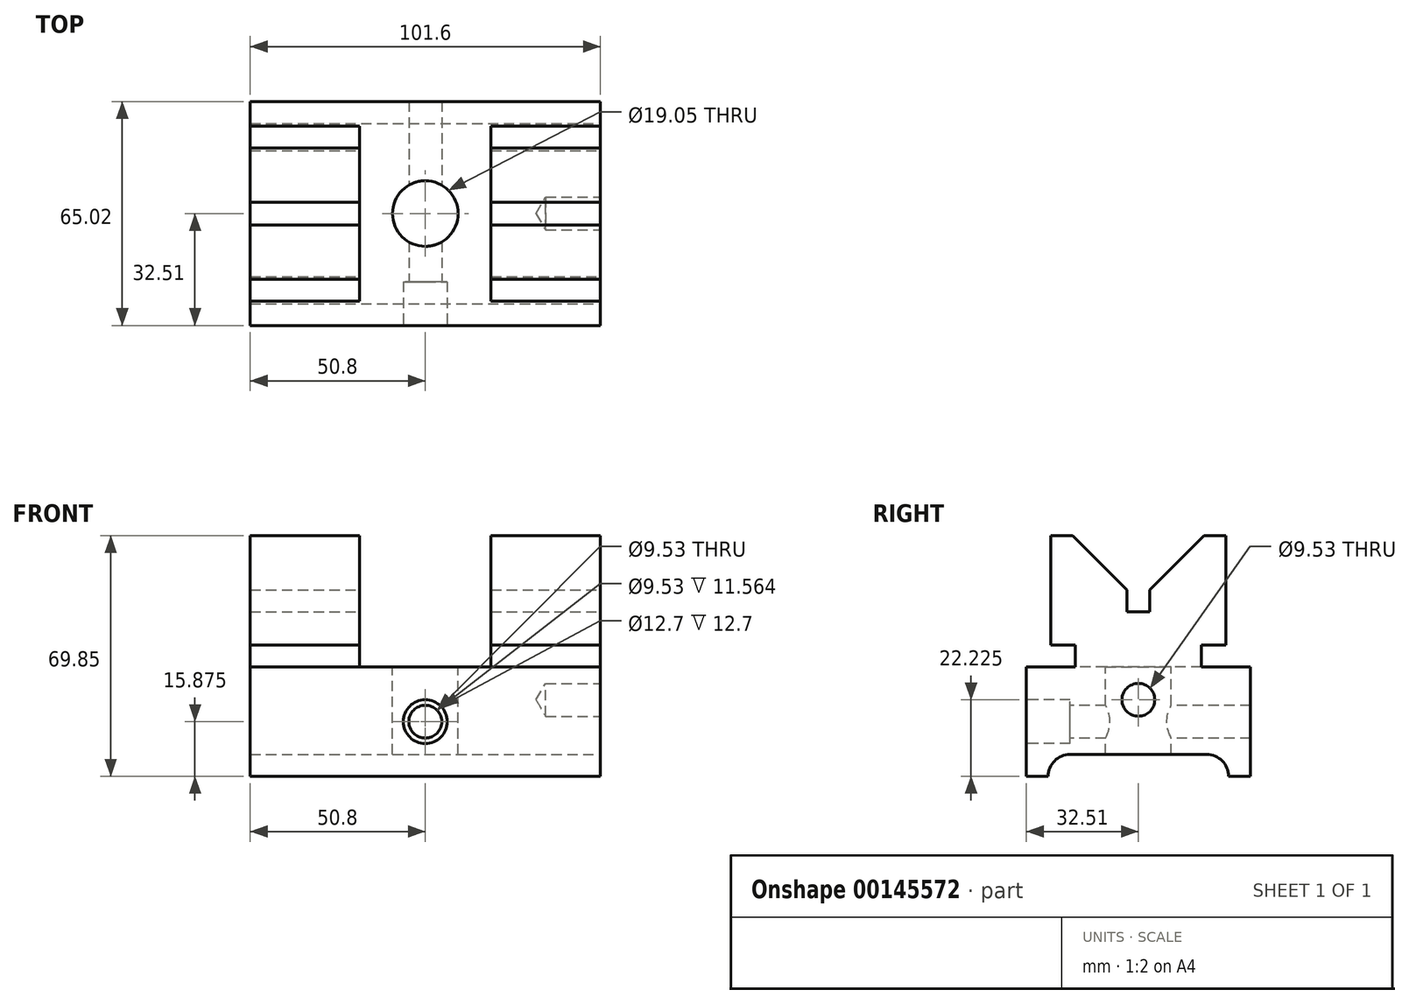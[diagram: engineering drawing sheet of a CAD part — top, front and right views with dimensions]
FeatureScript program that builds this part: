
annotation { "Feature Type Name" : "Feature", "Feature Type Description" : "" }
export const myFeature = defineFeature(function(context is Context, id is Id, definition is map)
    precondition{}
    {
        {
            var Q0;
            Q0=qCreatedBy(makeId("Right.planeOp"),FACE);
            var sketch = newSketch(context, id + "F0", { "sketchPlane" : qUnion([Q0])});
            skLineSegment(sketch, "E0", {"start": v(-32.51, 0) * mm, "end": v(-32.51, -31.75) * mm});
            skLineSegment(sketch, "E1", {"start": v(-32.51, -31.75) * mm, "end": v(-26.16, -31.75) * mm});
            skLineSegment(sketch, "E2", {"start": v(-26.16, -31.75) * mm, "end": v(-26.16, -31.75) * mm});
            skLineSegment(sketch, "E3", {"start": v(-19.81, -25.4) * mm, "end": v(19.81, -25.4) * mm});
            skLineSegment(sketch, "E4", {"start": v(26.16, -31.75) * mm, "end": v(26.16, -31.75) * mm});
            skLineSegment(sketch, "E5", {"start": v(26.16, -31.75) * mm, "end": v(32.51, -31.75) * mm});
            skLineSegment(sketch, "E6", {"start": v(32.51, -31.75) * mm, "end": v(32.51, 0) * mm});
            skLineSegment(sketch, "E7", {"start": v(32.51, 0) * mm, "end": v(18.29, 0) * mm});
            skLineSegment(sketch, "E8", {"start": v(18.29, 0) * mm, "end": v(18.29, 6.35) * mm});
            skLineSegment(sketch, "E9", {"start": v(-32.51, 0) * mm, "end": v(-18.29, 0) * mm});
            skLineSegment(sketch, "E10", {"start": v(-18.29, 0) * mm, "end": v(-18.29, 6.35) * mm});
            skPoint(sketch, "E11", {"position": v(0, -25.4) * mm});
            skLineSegment(sketch, "E12", {"start": v(18.29, 6.35) * mm, "end": v(25.4, 6.35) * mm});
            skLineSegment(sketch, "E13", {"start": v(25.4, 6.35) * mm, "end": v(25.4, 38.1) * mm});
            skLineSegment(sketch, "E14", {"start": v(25.4, 38.1) * mm, "end": v(19.05, 38.1) * mm});
            skLineSegment(sketch, "E15", {"start": v(19.05, 38.1) * mm, "end": v(3.3, 22.35) * mm});
            skLineSegment(sketch, "E16", {"start": v(3.3, 22.35) * mm, "end": v(3.3, 16) * mm});
            skLineSegment(sketch, "E17", {"start": v(3.3, 16) * mm, "end": v(-3.3, 16) * mm});
            skLineSegment(sketch, "E18", {"start": v(-3.3, 16) * mm, "end": v(-3.3, 22.35) * mm});
            skLineSegment(sketch, "E19", {"start": v(-3.3, 22.35) * mm, "end": v(-19.05, 38.1) * mm});
            skLineSegment(sketch, "E20", {"start": v(-19.05, 38.1) * mm, "end": v(-25.4, 38.1) * mm});
            skLineSegment(sketch, "E21", {"start": v(-25.4, 38.1) * mm, "end": v(-25.4, 6.35) * mm});
            skLineSegment(sketch, "E22", {"start": v(-25.4, 6.35) * mm, "end": v(-18.29, 6.35) * mm});
            skPoint(sketch, "E23", {"position": v(0, 16) * mm});
            skPoint(sketch, "E24.visualSharp", {"position": v(-26.16, -25.4) * mm});
            skArc(sketch, "E24.filletArc", {"start": v(-19.81, -25.4) * mm, "mid": v(-24.3, -27.26) * mm, "end": v(-26.16, -31.75) * mm});
            skPoint(sketch, "E25.visualSharp", {"position": v(26.16, -25.4) * mm});
            skArc(sketch, "E25.filletArc", {"start": v(26.16, -31.75) * mm, "mid": v(24.3, -27.26) * mm, "end": v(19.81, -25.4) * mm});
            skSolve(sketch);
        }
        {
            var Q0;
            Q0 = qSketchRegion(id + "F0", true);
            extrude(context, id + "F1", {"entities" : qUnion([Q0]), "oppositeDirection" : true, "depth" : 101.6 * mm});
        }
        {
            var Q0;
            Q0=makeQuery(id+"F1.opExtrude","CAP_FACE",FACE,{"disambiguationData":[OSD([sQuery(id+"F0.wireOp",EDGE,"E0"),sQuery(id+"F0.wireOp",EDGE,"E1"),sQuery(id+"F0.wireOp",EDGE,"E2"),sQuery(id+"F0.wireOp",EDGE,"E3"),sQuery(id+"F0.wireOp",EDGE,"E4"),sQuery(id+"F0.wireOp",EDGE,"E5"),sQuery(id+"F0.wireOp",EDGE,"E6"),sQuery(id+"F0.wireOp",EDGE,"E7"),sQuery(id+"F0.wireOp",EDGE,"E8"),sQuery(id+"F0.wireOp",EDGE,"E9"),sQuery(id+"F0.wireOp",EDGE,"E10"),sQuery(id+"F0.wireOp",EDGE,"E12"),sQuery(id+"F0.wireOp",EDGE,"E13"),sQuery(id+"F0.wireOp",EDGE,"E14"),sQuery(id+"F0.wireOp",EDGE,"E15"),sQuery(id+"F0.wireOp",EDGE,"E16"),sQuery(id+"F0.wireOp",EDGE,"E17"),sQuery(id+"F0.wireOp",EDGE,"E18"),sQuery(id+"F0.wireOp",EDGE,"E19"),sQuery(id+"F0.wireOp",EDGE,"E20"),sQuery(id+"F0.wireOp",EDGE,"E21"),sQuery(id+"F0.wireOp",EDGE,"E22")])],"isStart":true});
            var sketch = newSketch(context, id + "F2", { "sketchPlane" : qUnion([Q0])});
            skPoint(sketch, "E26", {"position": v(0, -9.52) * mm});
            skCircle(sketch, "E27", {"center": v(0, -9.52) * mm, "radius": 4.76 * mm});
            skSolve(sketch);
        }
        {
            var Q0;
            Q0=sQuery(id+"F2.wireOp",VERTEX,"E26");
            var Q1;
            Q1=makeQuery(id+"F1.opExtrude","SWEPT_BODY",BODY,{"disambiguationData":[OSD([sQuery(id+"F0.wireOp",EDGE,"E0"),sQuery(id+"F0.wireOp",EDGE,"E1"),sQuery(id+"F0.wireOp",EDGE,"E2"),sQuery(id+"F0.wireOp",EDGE,"E3"),sQuery(id+"F0.wireOp",EDGE,"E4"),sQuery(id+"F0.wireOp",EDGE,"E5"),sQuery(id+"F0.wireOp",EDGE,"E6"),sQuery(id+"F0.wireOp",EDGE,"E7"),sQuery(id+"F0.wireOp",EDGE,"E8"),sQuery(id+"F0.wireOp",EDGE,"E9"),sQuery(id+"F0.wireOp",EDGE,"E10"),sQuery(id+"F0.wireOp",EDGE,"E12"),sQuery(id+"F0.wireOp",EDGE,"E13"),sQuery(id+"F0.wireOp",EDGE,"E14"),sQuery(id+"F0.wireOp",EDGE,"E15"),sQuery(id+"F0.wireOp",EDGE,"E16"),sQuery(id+"F0.wireOp",EDGE,"E17"),sQuery(id+"F0.wireOp",EDGE,"E18"),sQuery(id+"F0.wireOp",EDGE,"E19"),sQuery(id+"F0.wireOp",EDGE,"E20"),sQuery(id+"F0.wireOp",EDGE,"E21"),sQuery(id+"F0.wireOp",EDGE,"E22")])]});
            hole(context, id + "F3", {"style" : HoleStyle.C_BORE, "endStyle" : HoleEndStyle.BLIND, "holeDiameter" : 9.52 * mm, "cBoreDiameter" : 9.52 * mm, "cBoreDepth" : 9.52 * mm, "holeDepth" : 15.88 * mm, "startFromSketch" : true, "locations" : qUnion([Q0]), "scope" : qUnion([Q1])});
        }
        {
            var Q0;
            Q0=makeQuery(id+"F1.opExtrude","SWEPT_FACE",FACE,{"disambiguationData":[OSD([sQuery(id+"F0.wireOp",EDGE,"E0")])]});
            var sketch = newSketch(context, id + "F4", { "sketchPlane" : qUnion([Q0])});
            skPoint(sketch, "E28", {"position": v(-50.8, -15.87) * mm});
            skCircle(sketch, "E29", {"center": v(-50.8, -15.87) * mm, "radius": 4.76 * mm});
            skSolve(sketch);
        }
        {
            var Q0;
            Q0=sQuery(id+"F4.wireOp",VERTEX,"E28");
            var Q1;
            Q1=makeQuery(id+"F1.opExtrude","SWEPT_BODY",BODY,{"disambiguationData":[OSD([sQuery(id+"F0.wireOp",EDGE,"E0"),sQuery(id+"F0.wireOp",EDGE,"E1"),sQuery(id+"F0.wireOp",EDGE,"E2"),sQuery(id+"F0.wireOp",EDGE,"E3"),sQuery(id+"F0.wireOp",EDGE,"E4"),sQuery(id+"F0.wireOp",EDGE,"E5"),sQuery(id+"F0.wireOp",EDGE,"E6"),sQuery(id+"F0.wireOp",EDGE,"E7"),sQuery(id+"F0.wireOp",EDGE,"E8"),sQuery(id+"F0.wireOp",EDGE,"E9"),sQuery(id+"F0.wireOp",EDGE,"E10"),sQuery(id+"F0.wireOp",EDGE,"E12"),sQuery(id+"F0.wireOp",EDGE,"E13"),sQuery(id+"F0.wireOp",EDGE,"E14"),sQuery(id+"F0.wireOp",EDGE,"E15"),sQuery(id+"F0.wireOp",EDGE,"E16"),sQuery(id+"F0.wireOp",EDGE,"E17"),sQuery(id+"F0.wireOp",EDGE,"E18"),sQuery(id+"F0.wireOp",EDGE,"E19"),sQuery(id+"F0.wireOp",EDGE,"E20"),sQuery(id+"F0.wireOp",EDGE,"E21"),sQuery(id+"F0.wireOp",EDGE,"E22")])]});
            hole(context, id + "F5", {"style" : HoleStyle.C_BORE, "endStyle" : HoleEndStyle.THROUGH, "holeDiameter" : 9.52 * mm, "cBoreDiameter" : 12.7 * mm, "cBoreDepth" : 12.7 * mm, "startFromSketch" : true, "locations" : qUnion([Q0]), "scope" : qUnion([Q1]), "isTappedThrough" : true});
        }
        {
            var Q0;
            Q0=makeQuery(id+"F1.opExtrude","SWEPT_FACE",FACE,{"disambiguationData":[OSD([sQuery(id+"F0.wireOp",EDGE,"E21")])]});
            var sketch = newSketch(context, id + "F6", { "sketchPlane" : qUnion([Q0])});
            skLineSegment(sketch, "E30.bottom", {"start": v(-69.85, 38.1) * mm, "end": v(-31.75, 38.1) * mm});
            skLineSegment(sketch, "E30.top", {"start": v(-69.85, 0) * mm, "end": v(-31.75, 0) * mm});
            skLineSegment(sketch, "E30.left", {"start": v(-69.85, 38.1) * mm, "end": v(-69.85, 0) * mm});
            skLineSegment(sketch, "E30.right", {"start": v(-31.75, 38.1) * mm, "end": v(-31.75, 0) * mm});
            skLineSegment(sketch, "E31", {"start": v(-50.8, 38.1) * mm, "end": v(-50.8, -31.75) * mm, "construction": true});
            skSolve(sketch);
        }
        {
            var Q0;
            Q0 = qSketchRegion(id + "F6", true);
            extrude(context, id + "F7", {"entities" : qUnion([Q0]), "operationType" : NewBodyOperationType.REMOVE, "endBound" : BoundingType.THROUGH_ALL, "oppositeDirection" : true, "depth" : 25.4 * mm});
        }
        {
            var Q0;
            Q0=makeQuery(id+"F7.boolean.opBoolean","MERGE",FACE,{"derivedFrom":[makeQuery(id+"F1.opExtrude","SWEPT_FACE",FACE,{"disambiguationData":[OSD([sQuery(id+"F0.wireOp",EDGE,"E7")])]}),makeQuery(id+"F1.opExtrude","SWEPT_FACE",FACE,{"disambiguationData":[OSD([sQuery(id+"F0.wireOp",EDGE,"E9")])]}),makeQuery(id+"F7.opExtrude","SWEPT_FACE",FACE,{"disambiguationData":[OSD([sQuery(id+"F6.wireOp",EDGE,"E30.top")])]})]});
            var sketch = newSketch(context, id + "F8", { "sketchPlane" : qUnion([Q0])});
            skPoint(sketch, "E32", {"position": v(-50.8, 0) * mm});
            skCircle(sketch, "E33", {"center": v(-50.8, 0) * mm, "radius": 9.53 * mm});
            skPoint(sketch, "E34", {"position": v(-50.8, 32.51) * mm});
            skLineSegment(sketch, "E35", {"start": v(-50.8, 32.51) * mm, "end": v(-50.8, -32.51) * mm, "construction": true});
            skSolve(sketch);
        }
        {
            var Q0;
            Q0 = qSketchRegion(id + "F8", true);
            extrude(context, id + "F9", {"entities" : qUnion([Q0]), "operationType" : NewBodyOperationType.REMOVE, "endBound" : BoundingType.THROUGH_ALL, "oppositeDirection" : true, "depth" : 25.4 * mm});
        }
    });
